# Revit family: JC KONTAKTER JCK237 DE
name_source: partatom
category: Specialty Equipment
units: mm (PartAtom-declared; Revit-internal decimal feet)

## family parameters
Cut with Voids When Loaded = No
Enable Cutting in Views = Yes
Host = Face
Maintain Annotation Orientation = Yes
Part Type = Normal
Room Calculation Point = No
Round Connector Dimension = Use Diameter
Shared = No

## types (1)
- JCK237
    Anzahl der mikroschalter = 2
    CE-kennzeichnung = https://jckontakter.se
    Deckel = Aluminum ENAW 6060 (schwarz)
    Deckel 2 = Aluminum ENAW 6060 (schwarz)
    Default Elevation = 800 mm  [stored 2.62467 ft]
    Description = JCK237 gehört zu einer Serie von Großflächentastern mit doppelten Tastflächen, die es ermöglichen, z.B. eine zusätzliche Tür oder ein Schloss zu schalten. Der JCK237 ist aus schwarzeloxiertem Aluminium mit weißen Endkappen gefertigt. Beide Tastflächen sind mit vier taktilen Rillen versehen und dienen als zusätzliche Orientierungshilfe für sehbehinderte Personen. So lässt sich leicht erfühlen, wo man drücken muss, um die Türöffnung zu aktivieren.
    Endkappen = POM Tenac C 4520 (weiss)
    Geringster nennstrom = 1mA/4 V DC
    Herstellungsland = Schweden
    Kern = Aluminum ENAW 6060
    Kunststoffstück = POM Tenac C 4520 (weiss)
    Manufacturer = JC kontakter
    Mikroschalter = Standard NO IP67
    Model = JCK237
    Nomineller nennstrom = 12 V - Resistive 6A Inductive L/R 5ms 6A, 24 V - Resistive 6A Inductive L/R 5ms 5A
    Produktgewicht = 0.397 kg.
    Technisches Produktblatt = https://grossflaechentaster.de
    URL = https://grossflaechentaster.de

note: [stored X ft] marks values corroborated as IEEE doubles in the binary element streams (Revit-internal decimal feet)

## geometry (parser evidence)
native form markers: Sweep x5
no freeform markers — native parametric forms only
